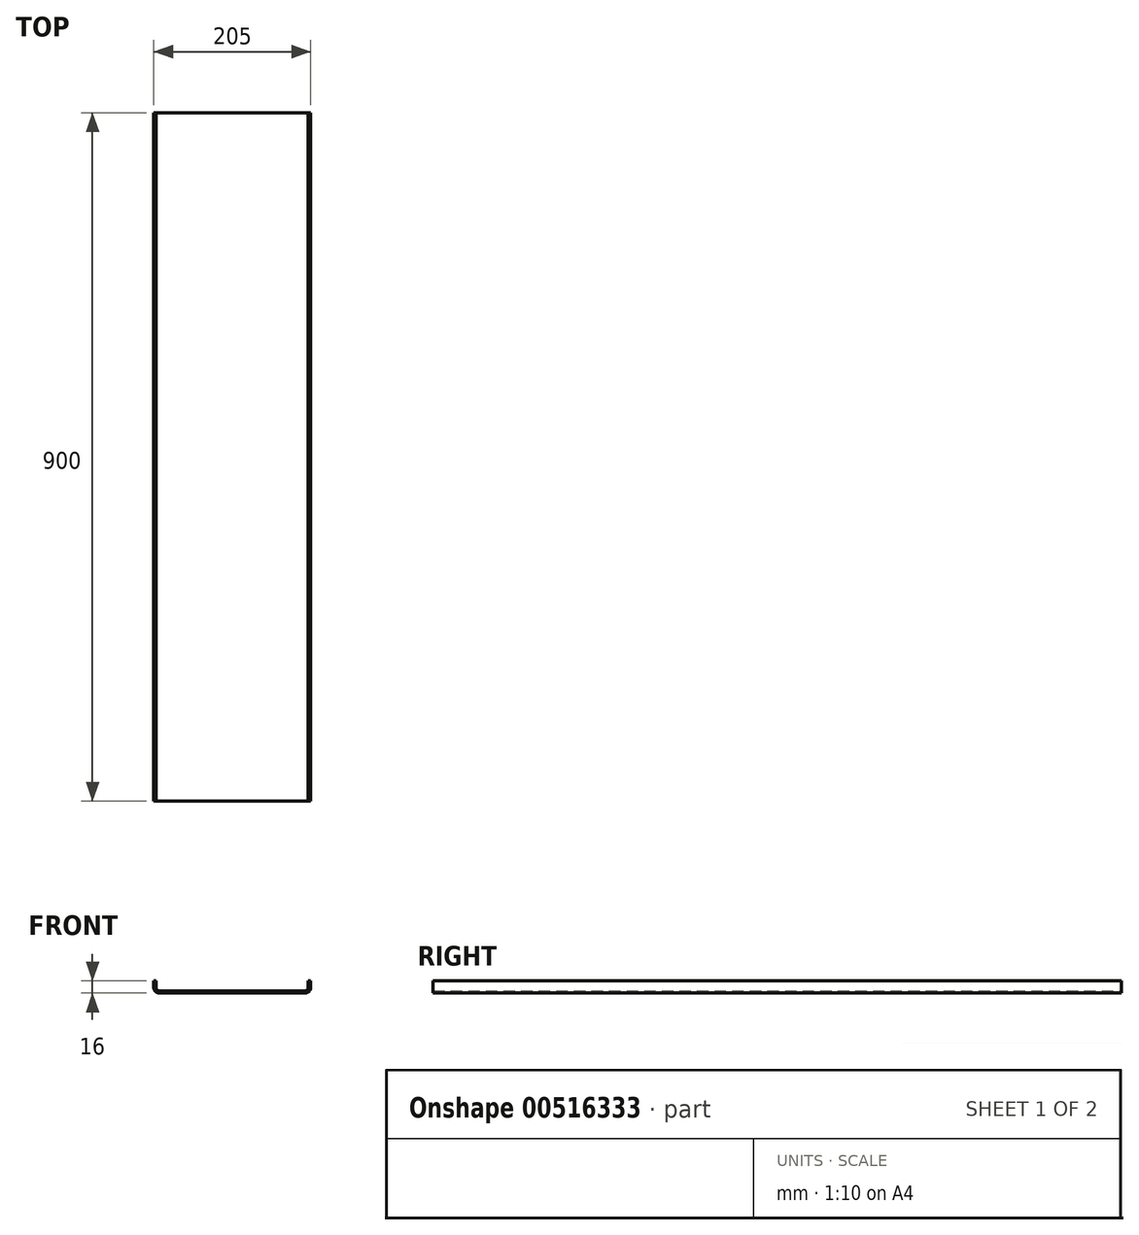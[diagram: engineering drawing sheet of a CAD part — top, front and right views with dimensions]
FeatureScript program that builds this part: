
annotation { "Feature Type Name" : "Feature", "Feature Type Description" : "" }
export const myFeature = defineFeature(function(context is Context, id is Id, definition is map)
    precondition{}
    {
        {
            var Q0;
            Q0=qCreatedBy(makeId("Front.planeOp"),FACE);
            var sketch = newSketch(context, id + "F0", { "sketchPlane" : qUnion([Q0])});
            skLineSegment(sketch, "E0.top", {"start": v(-102.5, -16) * mm, "end": v(102.5, -16) * mm});
            skLineSegment(sketch, "E0.left", {"start": v(-102.5, 0) * mm, "end": v(-102.5, -16) * mm});
            skLineSegment(sketch, "E0.right", {"start": v(102.5, 0) * mm, "end": v(102.5, -16) * mm});
            skPoint(sketch, "E0.middle", {"position": v(0, 0) * mm});
            skLineSegment(sketch, "E1.bottom", {"start": v(99.5, -13) * mm, "end": v(-99.5, -13) * mm});
            skLineSegment(sketch, "E1.left", {"start": v(99.5, -13) * mm, "end": v(99.5, 0) * mm});
            skLineSegment(sketch, "E1.right", {"start": v(-99.5, -13) * mm, "end": v(-99.5, 0) * mm});
            skLineSegment(sketch, "E2", {"start": v(-102.5, 0) * mm, "end": v(-99.5, 0) * mm});
            skPoint(sketch, "E1.top.end.orphan", {"position": v(-99.5, 13) * mm});
            skPoint(sketch, "E0.bottom.start.orphan", {"position": v(-102.5, 16) * mm});
            skPoint(sketch, "E3.orphan", {"position": v(102.5, 16) * mm});
            skPoint(sketch, "E4.orphan", {"position": v(99.5, 13) * mm});
            skLineSegment(sketch, "E5.trimOffspring", {"start": v(99.5, 0) * mm, "end": v(102.5, 0) * mm});
            skSolve(sketch);
        }
        {
            var Q0;
            Q0 = qSketchRegion(id + "F0", true);
            extrude(context, id + "F1", {"entities" : qUnion([Q0]), "endBound" : BoundingType.SYMMETRIC, "depth" : 900 * mm, "offsetDistance" : 25 * mm});
        }
        {
            var Q0;
            Q0=makeQuery(id+"F1.opExtrude","SWEPT_EDGE",EDGE,{"disambiguationData":[OSD([sQuery(id+"F0.wireOp",EDGE,"E1.bottom"),sQuery(id+"F0.wireOp",EDGE,"E1.right")])]});
            var Q1;
            Q1=makeQuery(id+"F1.opExtrude","SWEPT_EDGE",EDGE,{"disambiguationData":[OSD([sQuery(id+"F0.wireOp",EDGE,"E1.bottom"),sQuery(id+"F0.wireOp",EDGE,"E1.left")])]});
            fillet(context, id + "F2", {"entities" : qUnion([Q0, Q1]), "radius" : 4 * mm, "tangentPropagation" : true, "allowEdgeOverflow" : false});
        }
        {
            var Q0;
            Q0=makeQuery(id+"F1.opExtrude","SWEPT_EDGE",EDGE,{"disambiguationData":[OSD([sQuery(id+"F0.wireOp",EDGE,"E0.top"),sQuery(id+"F0.wireOp",EDGE,"E0.left")])]});
            var Q1;
            Q1=makeQuery(id+"F1.opExtrude","SWEPT_EDGE",EDGE,{"disambiguationData":[OSD([sQuery(id+"F0.wireOp",EDGE,"E0.top"),sQuery(id+"F0.wireOp",EDGE,"E0.right")])]});
            fillet(context, id + "F3", {"entities" : qUnion([Q0, Q1]), "radius" : 7 * mm, "tangentPropagation" : true, "allowEdgeOverflow" : false});
        }
    });
